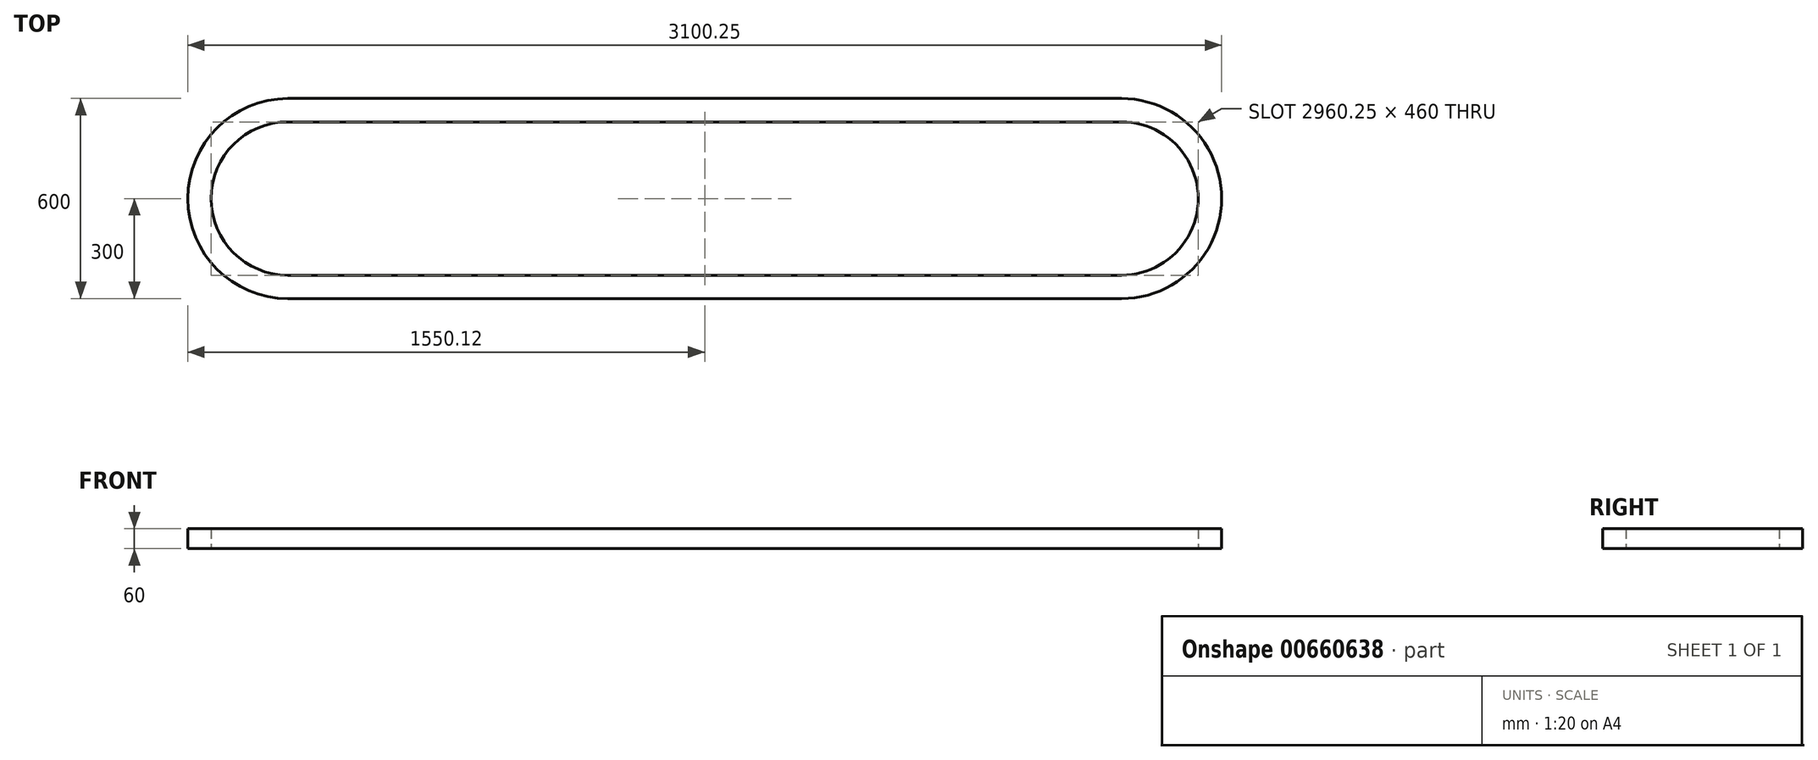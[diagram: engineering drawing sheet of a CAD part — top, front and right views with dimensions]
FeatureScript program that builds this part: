
annotation { "Feature Type Name" : "Feature", "Feature Type Description" : "" }
export const myFeature = defineFeature(function(context is Context, id is Id, definition is map)
    precondition{}
    {
        {
            var Q0;
            Q0=qCreatedBy(makeId("Top.planeOp"),FACE);
            var sketch = newSketch(context, id + "F0", { "sketchPlane" : qUnion([Q0])});
            skArc(sketch, "E0", {"start": v(0, 300) * mm, "mid": v(-300, 0) * mm, "end": v(0, -300) * mm});
            skArc(sketch, "E1", {"start": v(0, 230) * mm, "mid": v(-230, 0) * mm, "end": v(0, -230) * mm});
            skLineSegment(sketch, "E2", {"start": v(0, 0) * mm, "end": v(2500.25, 0) * mm});
            skArc(sketch, "E3", {"start": v(2500.25, -300) * mm, "mid": v(2800.25, 0.12) * mm, "end": v(2500, 300) * mm});
            skLineSegment(sketch, "E4", {"start": v(0, 300) * mm, "end": v(2500, 300) * mm});
            skLineSegment(sketch, "E5", {"start": v(2500.25, -300) * mm, "end": v(0, -300) * mm});
            skLineSegment(sketch, "E6", {"start": v(0, -230) * mm, "end": v(2500.25, -230) * mm});
            skLineSegment(sketch, "E7", {"start": v(0, 230) * mm, "end": v(2500, 230) * mm});
            skArc(sketch, "E8", {"start": v(2500.1, -230) * mm, "mid": v(2730.25, 0.05) * mm, "end": v(2500, 230) * mm});
            skSolve(sketch);
        }
        {
            var Q0;
            Q0=makeQuery(id+"F0.imprint","IMPRINT",FACE,{"disambiguationData":[TD([[makeQuery(id+"F0.imprint","IMPRINT",EDGE,{"derivedFrom":sQuery(id+"F0.wireOp",EDGE,"E0")}),1.0]])]});
            extrude(context, id + "F1", {"entities" : qUnion([Q0]), "depth" : 60 * mm, "offsetDistance" : 25 * mm});
        }
    });
